# Revit family: P300190-020
name_source: partatom
category: Lighting Fixtures
revit_build: Autodesk Revit 2014 (Build: 20130308_1515(x64)
units: mm (PartAtom-declared; Revit-internal decimal feet)

## types (1)
- P300190-020
    Apparent Load = 60 VA
    Assembly Code = D5020200
    Connector Description = Lighting Connector
    Default Elevation = 48 "
    Description = Axle Collection Two-Light Antique Bronze Vintage Style Bath Vanity Wall Light
    Features = Mix old and new for charming character with the Axle Collection 2-Light Antique Bronze Vintage Bath Vanity Light. The round backplate is coated in an antique bronze finish accented by golden satin brass vintage light bases. The working gooseneck arms provide customizable tilt adjustment.
Application: Mix old and new for charming character with the Axle Collection 2-Light Antique Bronze Vintage Bath Vanity Light ideal for any entryway, hallway, foyer, bedroom, sitting room, living room, or bathroom.
Style: Perfect for farmhouse, urban industrial, and vintage electric settings.
Finish: The round backplate is coated in an antique bronze finish accented by golden satin brass vintage light bases. The working gooseneck arms provide customizable tilt adjustment.
Materials: Constructed from steel to ensure a long product lifespan. Mount the light fixture facing up or down.
Glass: We recommend using vintage bulbs to enhance the wall light's timeless industrial aesthetic.
Bulbs: For ideal illumination, use 2 medium base bulbs that are sold separately (60w max - LED/CFL/incandescent)
compatible with dimmable bulbs.
Dimensions: Measures 16-inch width by 6-3/4-inch height by 6-inch depth.
Certifications: cULus damp location listed.
Pairs With: Pairs with a variety of Progress Lighting fixtures.
Warranty: Our 1-Year Limited Warranty guarantees your complete satisfaction with your purchase and includes after-sales customer service support.
    Fixture distribution = Direct
    Glass = Paint - Hubbell - White Texture
    Gold = Hubbell - Gold
    Housing Material = Paint - Hubbell - Textured Camera Black
    Lamp = LED/CFL/incandescent
    Load Classification = Lighting
    Manufacturer = Progress Lighting
    Model = P300190-020
    Power Factor = 1
    Product Documentation Link = https://hubbellcdn.com
    Product Link = https://www.hubbell.com
    URL = https://www.hubbell.com
    Voltage = 120 V
    Warranty = 1 year Warranty
    Wattage Comments = 60W
    Watts = 60 W

## geometry (parser evidence)
native form markers: Sweep x4
no freeform markers — native parametric forms only
